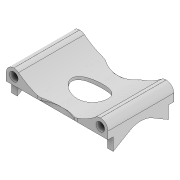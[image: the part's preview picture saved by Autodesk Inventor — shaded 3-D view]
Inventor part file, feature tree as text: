
AUTODESK INVENTOR PART (.ipt)
format: ipt  version: 2020 (Build 240168000, 168)  size: 314,880 bytes
history: native  units: mm
features: extrude x9, sketch x7, fillet x5, projected_geometry x4, mirror x2, plane x1
ambient origin geometry x8: Origin, YZ Plane, XZ Plane, XY Plane, X Axis, Y Axis, Z Axis, Center Point
bodies: Solid1 (feature_tree)
feature tree (28):
  extrude  "Extrusion1"  Depth=6.0mm
  extrude  "Extrusion2"  Depth=10.0mm TaperAngle=0.0deg
  extrude  "Extrusion3"  Depth=2.05mm TaperAngle=0.0deg
  mirror  "Mirror1"
  extrude  "Extrusion5"  Depth=8.0mm
  fillet  "Fillet3"  Radius=5.0mm
  plane  "Work Plane1"
  mirror  "Mirror2"
  extrude  "Extrusion7"  TaperAngle=0.0deg  [1 undecoded]
  extrude  "Extrusion8"  TaperAngle=180.0deg  [1 undecoded]
  fillet  "Fillet4"  [1 undecoded]
  fillet  "Fillet5"  Radius=200.0mm
  sketch  "Sketch9"  dims[d24=3.0mm d25=180.0deg d26=0.0mm d27=0.0mm d28=200.0mm]
  extrude  "Extrusion9"  Depth=3.0mm
  extrude  "Extrusion10"  Depth=10.0mm TaperAngle=0.0deg
  fillet  "Fillet6"  Radius=1.5mm
  extrude  "Extrusion11"  Depth=3.0mm
  fillet  "Fillet7"  Radius=1.5mm
  sketch  "Sketch1"  dims[d0=3.4mm d1=6.0mm]
  sketch  "Sketch3"  dims[d2=26.0mm d3=0.0mm d8=10.0mm d9=0.0mm]
  sketch  "Sketch5"  dims[d10=5.0mm d11=2.05mm d12=0.0mm]
  sketch  "Sketch7"  dims[d19=2.3mm d20=8.0mm d21=5.0mm]
  projected_geometry  "Projected Loop2"
  sketch  "Sketch8"  dims[d22=3.0mm d23=0.0mm]
  projected_geometry  "Projected Loop3"
  projected_geometry  "Projected Loop4"
  sketch  "Sketch10"  dims[d31=17.1mm d32=1.5mm d33=10.0mm d34=0.0mm d35=1.5mm d36=0.0mm d37=1.5mm d38=1.5mm d39=1.1mm d40=1.1mm d41=3.0mm d42=10.0mm d43=0.0mm d44=0.0mm d45=0.0mm d46=3.0mm d47=10.0mm d48=10.0mm d49=26.0mm d50=5.0mm d51=0.0mm d52=0.0mm d53=3.0mm]
  projected_geometry  "Projected Loop5"
note: 3 required parameter values undecoded (feature->parameter linkage not recoverable at this tier; creation-order binding heuristic only, values carry confidence <= 0.55)
